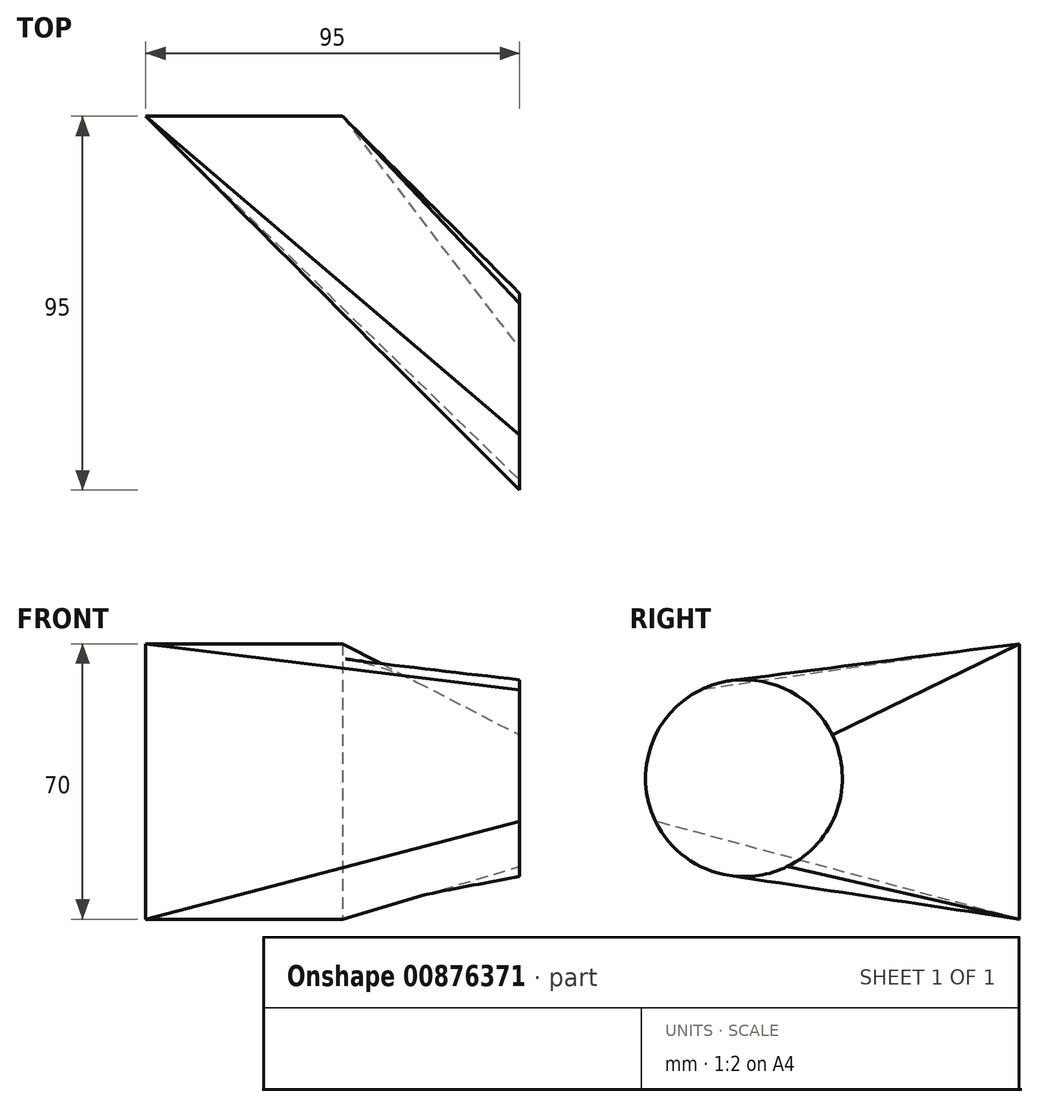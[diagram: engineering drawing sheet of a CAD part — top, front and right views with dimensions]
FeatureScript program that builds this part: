
annotation { "Feature Type Name" : "Feature", "Feature Type Description" : "" }
export const myFeature = defineFeature(function(context is Context, id is Id, definition is map)
    precondition{}
    {
        {
            var Q0;
            Q0=qCreatedBy(makeId("Front.planeOp"),FACE);
            var sketch = newSketch(context, id + "F0", { "sketchPlane" : qUnion([Q0])});
            skLineSegment(sketch, "E0.bottom", {"start": v(-45, 70) * mm, "end": v(-95, 70) * mm});
            skLineSegment(sketch, "E0.top", {"start": v(-45, 0) * mm, "end": v(-95, 0) * mm});
            skLineSegment(sketch, "E0.left", {"start": v(-45, 70) * mm, "end": v(-45, 0) * mm});
            skLineSegment(sketch, "E0.right", {"start": v(-95, 70) * mm, "end": v(-95, 0) * mm});
            skPoint(sketch, "E0.middle", {"position": v(-70, 35) * mm});
            skSolve(sketch);
        }
        {
            var Q0;
            Q0=qCreatedBy(makeId("Right.planeOp"),FACE);
            var sketch = newSketch(context, id + "F1", { "sketchPlane" : qUnion([Q0])});
            skCircle(sketch, "E1", {"center": v(-70, 35.83) * mm, "radius": 25 * mm});
            skSolve(sketch);
        }
        {
            var Q0;
            Q0 = qSketchRegion(id + "F0", true);
            var Q1;
            Q1 = qSketchRegion(id + "F1", true);
            loft(context, id + "F2", {"sheetProfilesArray" : [{ "sheetProfileEntities" : qUnion([Q0]) }, { "sheetProfileEntities" : qUnion([Q1]) }]});
        }
    });
